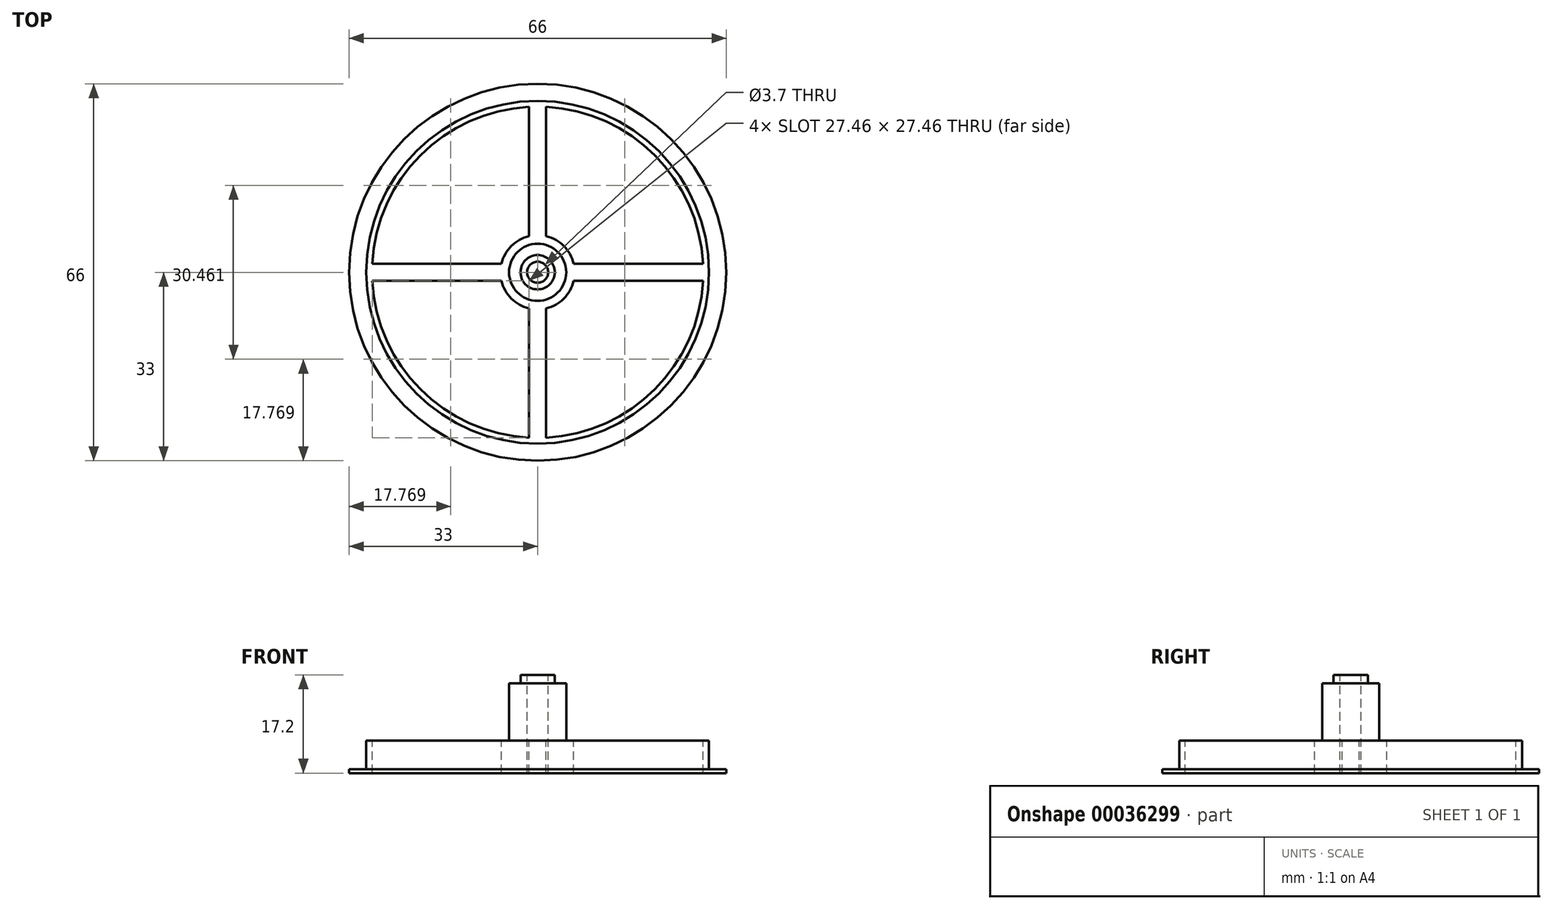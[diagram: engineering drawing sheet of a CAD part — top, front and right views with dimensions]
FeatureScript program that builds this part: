
annotation { "Feature Type Name" : "Feature", "Feature Type Description" : "" }
export const myFeature = defineFeature(function(context is Context, id is Id, definition is map)
    precondition{}
    {
        {
            var Q0;
            Q0=qCreatedBy(makeId("Top.planeOp"),FACE);
            var sketch = newSketch(context, id + "F0", { "sketchPlane" : qUnion([Q0])});
            skCircle(sketch, "E0", {"center": v(0, 0) * mm, "radius": 30 * mm});
            skSolve(sketch);
        }
        {
            var Q0;
            Q0=makeQuery(id+"F0.imprint","IMPRINT",FACE,{"disambiguationData":[TD([[makeQuery(id+"F0.imprint","IMPRINT",EDGE,{"derivedFrom":sQuery(id+"F0.wireOp",EDGE,"E0")}),1.0]])]});
            extrude(context, id + "F1", {"entities" : qUnion([Q0]), "depth" : 5 * mm});
        }
        {
            var Q0;
            Q0=makeQuery(id+"F1.opExtrude","CAP_FACE",FACE,{"disambiguationData":[OSD([sQuery(id+"F0.wireOp",EDGE,"E0")])],"isStart":false});
            var sketch = newSketch(context, id + "F2", { "sketchPlane" : qUnion([Q0])});
            skCircle(sketch, "E1", {"center": v(0, 0) * mm, "radius": 5 * mm});
            skSolve(sketch);
        }
        {
            var Q0;
            Q0=makeQuery(id+"F2.imprint","IMPRINT",FACE,{"disambiguationData":[TD([[makeQuery(id+"F2.imprint","IMPRINT",EDGE,{"derivedFrom":sQuery(id+"F2.wireOp",EDGE,"E1")}),1.0]])]});
            extrude(context, id + "F3", {"entities" : qUnion([Q0]), "operationType" : NewBodyOperationType.ADD, "depth" : 10 * mm});
        }
        {
            var Q0;
            Q0=makeQuery(id+"F3.opExtrude","CAP_FACE",FACE,{"disambiguationData":[OSD([sQuery(id+"F2.wireOp",EDGE,"E1")])],"isStart":false});
            var sketch = newSketch(context, id + "F4", { "sketchPlane" : qUnion([Q0])});
            skCircle(sketch, "E2", {"center": v(0, 0) * mm, "radius": 1.85 * mm});
            skSolve(sketch);
        }
        {
            var Q0;
            Q0=qSketchRegion(id+"F4",true);
            extrude(context, id + "F5", {"entities" : qUnion([Q0]), "operationType" : NewBodyOperationType.REMOVE, "endBound" : BoundingType.UP_TO_NEXT, "oppositeDirection" : true, "depth" : 25 * mm});
        }
        {
            var Q0;
            Q0=makeQuery(id+"F3.opExtrude","CAP_FACE",FACE,{"disambiguationData":[OSD([sQuery(id+"F2.wireOp",EDGE,"E1")])],"isStart":false});
            var sketch = newSketch(context, id + "F6", { "sketchPlane" : qUnion([Q0])});
            skCircle(sketch, "E3", {"center": v(0, 0) * mm, "radius": 3 * mm});
            skSolve(sketch);
        }
        {
            var Q0;
            Q0=makeQuery(id+"F6.imprint","IMPRINT",FACE,{"disambiguationData":[TD([[makeQuery(id+"F6.imprint","IMPRINT",EDGE,{"derivedFrom":sQuery(id+"F6.wireOp",EDGE,"E3")}),1.0]])]});
            extrude(context, id + "F7", {"entities" : qUnion([Q0]), "operationType" : NewBodyOperationType.ADD, "depth" : 1.5 * mm});
        }
        {
            var Q0;
            Q0=makeQuery(id+"F1.opExtrude","CAP_FACE",FACE,{"disambiguationData":[OSD([sQuery(id+"F0.wireOp",EDGE,"E0")])],"isStart":false});
            var sketch = newSketch(context, id + "F8", { "sketchPlane" : qUnion([Q0])});
            skCircle(sketch, "E4", {"center": v(0, 0) * mm, "radius": 29 * mm});
            skCircle(sketch, "E5", {"center": v(0, 0) * mm, "radius": 6.5 * mm});
            skLineSegment(sketch, "E6", {"start": v(0, -6.5) * mm, "end": v(0, -29) * mm, "construction": true});
            skLineSegment(sketch, "E7", {"start": v(-6.5, 0) * mm, "end": v(-29, 0) * mm, "construction": true});
            skLineSegment(sketch, "E8", {"start": v(0, 6.5) * mm, "end": v(0, 29) * mm, "construction": true});
            skLineSegment(sketch, "E9", {"start": v(6.5, 0) * mm, "end": v(29, 0) * mm, "construction": true});
            skLineSegment(sketch, "E10.0", {"start": v(1.5, 6.32) * mm, "end": v(1.5, 28.96) * mm});
            skLineSegment(sketch, "E11.0", {"start": v(-1.5, 6.32) * mm, "end": v(-1.5, 28.96) * mm});
            skLineSegment(sketch, "E12", {"start": v(1.5, -6.32) * mm, "end": v(1.5, -28.96) * mm});
            skLineSegment(sketch, "E13", {"start": v(-1.5, -6.32) * mm, "end": v(-1.5, -28.96) * mm});
            skLineSegment(sketch, "E14.0", {"start": v(6.32, 1.5) * mm, "end": v(28.96, 1.5) * mm});
            skLineSegment(sketch, "E15.0", {"start": v(6.32, -1.5) * mm, "end": v(28.96, -1.5) * mm});
            skLineSegment(sketch, "E16", {"start": v(-6.32, 1.5) * mm, "end": v(-28.96, 1.5) * mm});
            skLineSegment(sketch, "E17", {"start": v(-6.32, -1.5) * mm, "end": v(-28.96, -1.5) * mm});
            skSolve(sketch);
        }
        {
            var Q0;
            {var subQ1=sQuery(id+"F8.wireOp",EDGE,"E10.0");Q0=makeQuery(id+"F8.imprint","IMPRINT",FACE,{"disambiguationData":[TD([[makeQuery(id+"F8.imprint","IMPRINT",EDGE,{"derivedFrom":subQ1}),-1.0]])]});}
            var Q1;
            {var subQ2=sQuery(id+"F8.wireOp",EDGE,"E11.0");Q1=makeQuery(id+"F8.imprint","IMPRINT",FACE,{"disambiguationData":[TD([[makeQuery(id+"F8.imprint","IMPRINT",EDGE,{"derivedFrom":subQ2}),1.0]])]});}
            var Q2;
            {var subQ1=sQuery(id+"F8.wireOp",EDGE,"E13");Q2=makeQuery(id+"F8.imprint","IMPRINT",FACE,{"disambiguationData":[TD([[makeQuery(id+"F8.imprint","IMPRINT",EDGE,{"derivedFrom":subQ1}),-1.0]])]});}
            var Q3;
            {var subQ0=sQuery(id+"F8.wireOp",EDGE,"E12");Q3=makeQuery(id+"F8.imprint","IMPRINT",FACE,{"disambiguationData":[TD([[makeQuery(id+"F8.imprint","IMPRINT",EDGE,{"derivedFrom":subQ0}),1.0]])]});}
            extrude(context, id + "F9", {"entities" : qUnion([Q0, Q1, Q2, Q3]), "operationType" : NewBodyOperationType.REMOVE, "endBound" : BoundingType.UP_TO_NEXT, "oppositeDirection" : true, "depth" : 25 * mm});
        }
        {
            var Q0;
            Q0=makeQuery(id+"F1.opExtrude","CAP_FACE",FACE,{"disambiguationData":[OSD([sQuery(id+"F0.wireOp",EDGE,"E0")])],"isStart":true});
            var sketch = newSketch(context, id + "F10", { "sketchPlane" : qUnion([Q0])});
            skCircle(sketch, "E18", {"center": v(0, 0) * mm, "radius": 33 * mm});
            skSolve(sketch);
        }
        {
            var Q0;
            Q0=makeQuery(id+"F10.imprint","IMPRINT",FACE,{"disambiguationData":[TD([[makeQuery(id+"F10.imprint","IMPRINT",EDGE,{"derivedFrom":sQuery(id+"F10.wireOp",EDGE,"E18")}),1.0]])]});
            var Q1;
            {var subQ0=sQuery(id+"F0.wireOp",EDGE,"E0");Q1=makeQuery(id+"F10.imprint","IMPRINT",FACE,{"disambiguationData":[TD([[makeQuery(id+"F10.imprint","IMPRINT",EDGE,{"derivedFrom":makeQuery(id+"F1.opExtrude","CAP_EDGE",EDGE,{"disambiguationData":[OSD([subQ0])],"isStart":true})}),-1.0]])]});}
            extrude(context, id + "F11", {"entities" : qUnion([Q0, Q1]), "operationType" : NewBodyOperationType.ADD, "depth" : 0.7 * mm});
        }
    });
